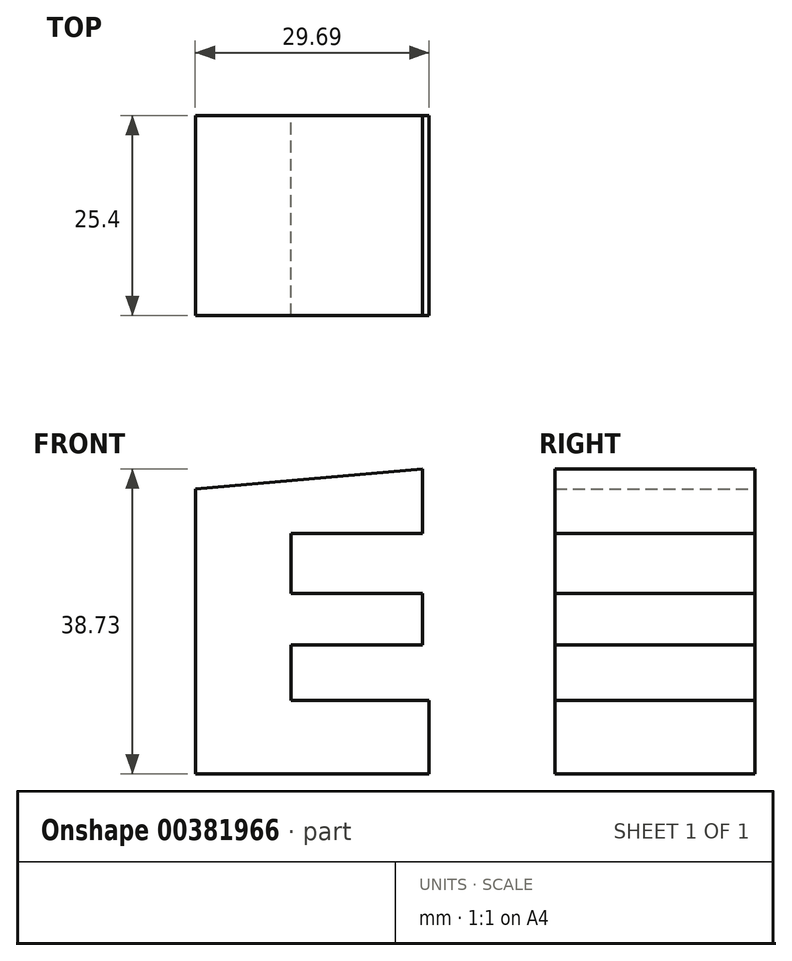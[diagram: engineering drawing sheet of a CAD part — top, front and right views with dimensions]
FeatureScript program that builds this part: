
annotation { "Feature Type Name" : "Feature", "Feature Type Description" : "" }
export const myFeature = defineFeature(function(context is Context, id is Id, definition is map)
    precondition{}
    {
        {
            var Q0;
            Q0=qCreatedBy(makeId("Front.planeOp"),FACE);
            var sketch = newSketch(context, id + "F0", { "sketchPlane" : qUnion([Q0])});
            skLineSegment(sketch, "E0", {"start": v(-49.76, 40.15) * mm, "end": v(-49.76, 3.96) * mm});
            skLineSegment(sketch, "E1", {"start": v(-49.76, 3.96) * mm, "end": v(-20.07, 3.96) * mm});
            skLineSegment(sketch, "E2", {"start": v(-20.07, 3.96) * mm, "end": v(-20.07, 13.29) * mm});
            skLineSegment(sketch, "E3", {"start": v(-20.07, 13.29) * mm, "end": v(-37.6, 13.29) * mm});
            skLineSegment(sketch, "E4", {"start": v(-37.6, 13.29) * mm, "end": v(-37.6, 20.36) * mm});
            skLineSegment(sketch, "E5", {"start": v(-37.6, 20.36) * mm, "end": v(-20.07, 20.36) * mm});
            skLineSegment(sketch, "E6", {"start": v(-20.92, 20.36) * mm, "end": v(-20.92, 26.86) * mm});
            skLineSegment(sketch, "E7", {"start": v(-20.92, 26.86) * mm, "end": v(-37.6, 26.86) * mm});
            skLineSegment(sketch, "E8", {"start": v(-37.6, 26.86) * mm, "end": v(-37.6, 34.5) * mm});
            skLineSegment(sketch, "E9", {"start": v(-37.6, 34.5) * mm, "end": v(-20.92, 34.5) * mm});
            skLineSegment(sketch, "E10", {"start": v(-20.92, 34.5) * mm, "end": v(-20.92, 42.7) * mm});
            skLineSegment(sketch, "E11", {"start": v(-20.92, 42.7) * mm, "end": v(-49.76, 40.15) * mm});
            skSolve(sketch);
        }
        {
            var Q0;
            Q0=makeQuery(id+"F0.imprint","IMPRINT",FACE,{"disambiguationData":[TD([[makeQuery(id+"F0.imprint","IMPRINT",EDGE,{"derivedFrom":sQuery(id+"F0.wireOp",EDGE,"E0")}),1.0]])]});
            extrude(context, id + "F1", {"entities" : qUnion([Q0]), "depth" : 25.4 * mm, "offsetDistance" : 25.4 * mm});
        }
    });
